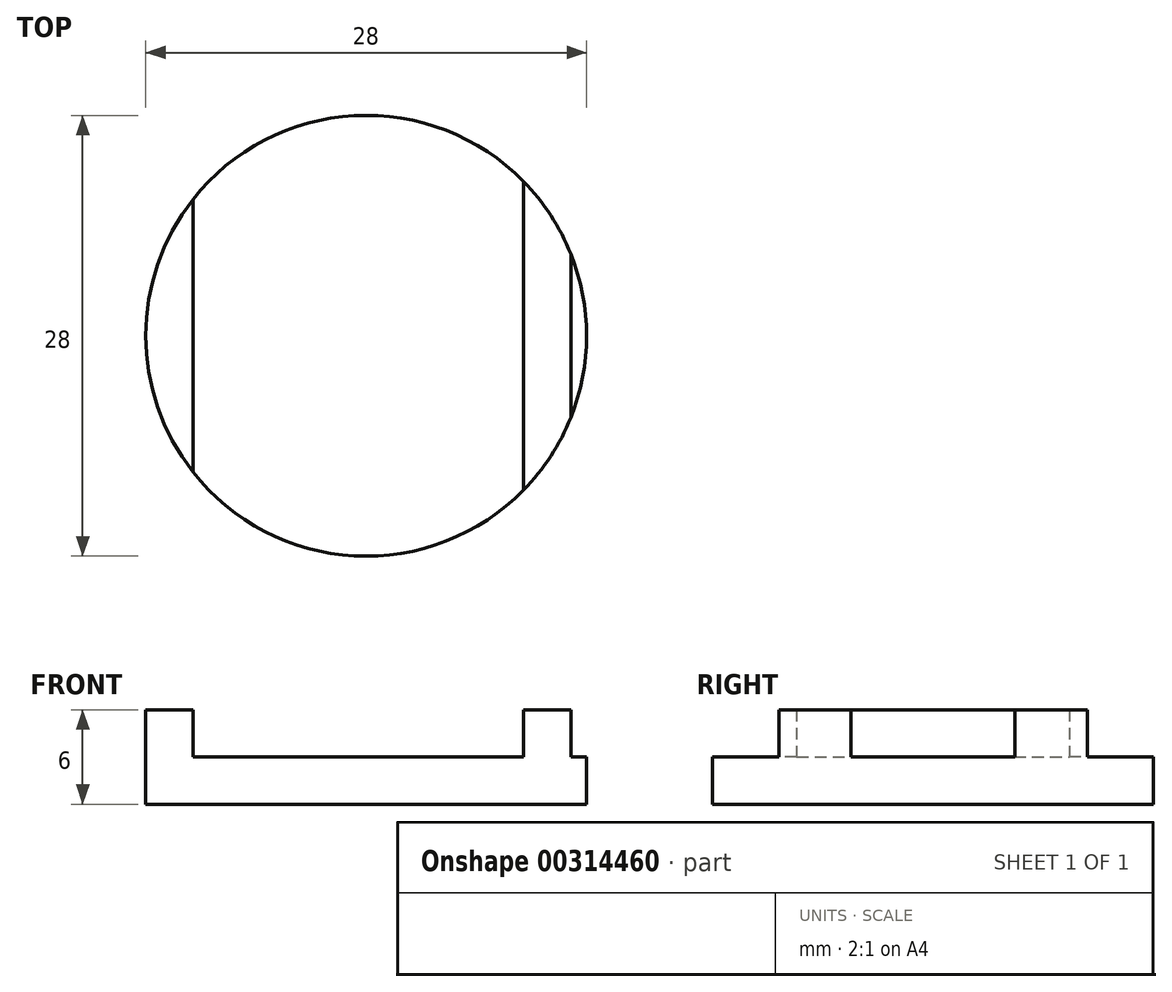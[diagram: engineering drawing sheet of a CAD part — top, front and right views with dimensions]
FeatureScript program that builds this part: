
annotation { "Feature Type Name" : "Feature", "Feature Type Description" : "" }
export const myFeature = defineFeature(function(context is Context, id is Id, definition is map)
    precondition{}
    {
        {
            var Q0;
            Q0=qCreatedBy(makeId("Top.planeOp"),FACE);
            var sketch = newSketch(context, id + "F0", { "sketchPlane" : qUnion([Q0])});
            skCircle(sketch, "E0", {"center": v(0, 0) * mm, "radius": 14 * mm});
            skSolve(sketch);
        }
        {
            var Q0;
            Q0=makeQuery(id+"F0.imprint","IMPRINT",FACE,{"disambiguationData":[TD([[makeQuery(id+"F0.imprint","IMPRINT",EDGE,{"derivedFrom":sQuery(id+"F0.wireOp",EDGE,"E0")}),1.0]])]});
            extrude(context, id + "F1", {"entities" : qUnion([Q0]), "depth" : 3 * mm});
        }
        {
            var Q0;
            Q0=makeQuery(id+"F1.opExtrude","CAP_FACE",FACE,{"disambiguationData":[OSD([sQuery(id+"F0.wireOp",EDGE,"E0")])],"isStart":false});
            var sketch = newSketch(context, id + "F2", { "sketchPlane" : qUnion([Q0])});
            skLineSegment(sketch, "E1.bottom", {"start": v(-11, -14) * mm, "end": v(-14, -14) * mm});
            skLineSegment(sketch, "E1.top", {"start": v(-11, 14) * mm, "end": v(-14, 14) * mm});
            skLineSegment(sketch, "E1.left", {"start": v(-11, -14) * mm, "end": v(-11, 14) * mm});
            skLineSegment(sketch, "E1.right", {"start": v(-14, -14) * mm, "end": v(-14, 14) * mm});
            skPoint(sketch, "E1.middle", {"position": v(-12.5, 0) * mm});
            skLineSegment(sketch, "E2.1.0.0", {"start": v(-8, -14) * mm, "end": v(-11, -14) * mm});
            skLineSegment(sketch, "E2.1.0.1", {"start": v(-8, 14) * mm, "end": v(-11, 14) * mm});
            skLineSegment(sketch, "E2.1.0.2", {"start": v(-8, -14) * mm, "end": v(-8, 14) * mm});
            skPoint(sketch, "E2.1.0.4", {"position": v(-9.5, 0) * mm});
            skLineSegment(sketch, "E2.2.0.0", {"start": v(-5, -14) * mm, "end": v(-8, -14) * mm});
            skLineSegment(sketch, "E2.2.0.1", {"start": v(-5, 14) * mm, "end": v(-8, 14) * mm});
            skLineSegment(sketch, "E2.2.0.2", {"start": v(-5, -14) * mm, "end": v(-5, 14) * mm});
            skLineSegment(sketch, "E2.2.0.3", {"start": v(-8, -14) * mm, "end": v(-8, 14) * mm});
            skPoint(sketch, "E2.2.0.4", {"position": v(-6.5, 0) * mm});
            skLineSegment(sketch, "E2.direction1", {"start": v(-14, -14) * mm, "end": v(-11, -14) * mm, "construction": true});
            skLineSegment(sketch, "E3.0.3.0", {"start": v(-2, -14) * mm, "end": v(-5, -14) * mm});
            skLineSegment(sketch, "E3.3.3.0", {"start": v(-2, 14) * mm, "end": v(-5, 14) * mm});
            skLineSegment(sketch, "E3.6.3.0", {"start": v(-2, -14) * mm, "end": v(-2, 14) * mm});
            skPoint(sketch, "E3.12.3.0", {"position": v(-3.5, 0) * mm});
            skLineSegment(sketch, "E3.0.4.0", {"start": v(1, -14) * mm, "end": v(-2, -14) * mm});
            skLineSegment(sketch, "E3.3.4.0", {"start": v(1, 14) * mm, "end": v(-2, 14) * mm});
            skLineSegment(sketch, "E3.6.4.0", {"start": v(1, -14) * mm, "end": v(1, 14) * mm});
            skLineSegment(sketch, "E3.9.4.0", {"start": v(-2, -14) * mm, "end": v(-2, 14) * mm});
            skPoint(sketch, "E3.12.4.0", {"position": v(-0.5, 0) * mm});
            skLineSegment(sketch, "E3.0.5.0", {"start": v(4, -14) * mm, "end": v(1, -14) * mm});
            skLineSegment(sketch, "E3.3.5.0", {"start": v(4, 14) * mm, "end": v(1, 14) * mm});
            skLineSegment(sketch, "E3.6.5.0", {"start": v(4, -14) * mm, "end": v(4, 14) * mm});
            skLineSegment(sketch, "E3.9.5.0", {"start": v(1, -14) * mm, "end": v(1, 14) * mm});
            skPoint(sketch, "E3.12.5.0", {"position": v(2.5, 0) * mm});
            skLineSegment(sketch, "E3.0.6.0", {"start": v(7, -14) * mm, "end": v(4, -14) * mm});
            skLineSegment(sketch, "E3.3.6.0", {"start": v(7, 14) * mm, "end": v(4, 14) * mm});
            skLineSegment(sketch, "E3.6.6.0", {"start": v(7, -14) * mm, "end": v(7, 14) * mm});
            skLineSegment(sketch, "E3.9.6.0", {"start": v(4, -14) * mm, "end": v(4, 14) * mm});
            skPoint(sketch, "E3.12.6.0", {"position": v(5.5, 0) * mm});
            skLineSegment(sketch, "E3.0.7.0", {"start": v(10, -14) * mm, "end": v(7, -14) * mm});
            skLineSegment(sketch, "E3.3.7.0", {"start": v(10, 14) * mm, "end": v(7, 14) * mm});
            skLineSegment(sketch, "E3.6.7.0", {"start": v(10, -14) * mm, "end": v(10, 14) * mm});
            skLineSegment(sketch, "E3.9.7.0", {"start": v(7, -14) * mm, "end": v(7, 14) * mm});
            skPoint(sketch, "E3.12.7.0", {"position": v(8.5, 0) * mm});
            skLineSegment(sketch, "E4.0.8.0", {"start": v(13, -14) * mm, "end": v(10, -14) * mm});
            skLineSegment(sketch, "E4.3.8.0", {"start": v(13, 14) * mm, "end": v(10, 14) * mm});
            skLineSegment(sketch, "E4.6.8.0", {"start": v(13, -14) * mm, "end": v(13, 14) * mm});
            skPoint(sketch, "E4.12.8.0", {"position": v(11.5, 0) * mm});
            skLineSegment(sketch, "E4.0.9.0", {"start": v(16, -14) * mm, "end": v(13, -14) * mm});
            skLineSegment(sketch, "E4.3.9.0", {"start": v(16, 14) * mm, "end": v(13, 14) * mm});
            skLineSegment(sketch, "E4.6.9.0", {"start": v(16, -14) * mm, "end": v(16, 14) * mm});
            skLineSegment(sketch, "E4.9.9.0", {"start": v(13, -14) * mm, "end": v(13, 14) * mm});
            skPoint(sketch, "E4.12.9.0", {"position": v(14.5, 0) * mm});
            skLineSegment(sketch, "E4.0.10.0", {"start": v(19, -14) * mm, "end": v(16, -14) * mm});
            skLineSegment(sketch, "E4.3.10.0", {"start": v(19, 14) * mm, "end": v(16, 14) * mm});
            skLineSegment(sketch, "E4.6.10.0", {"start": v(19, -14) * mm, "end": v(19, 14) * mm});
            skLineSegment(sketch, "E4.9.10.0", {"start": v(16, -14) * mm, "end": v(16, 14) * mm});
            skPoint(sketch, "E4.12.10.0", {"position": v(17.5, 0) * mm});
            skLineSegment(sketch, "E4.0.11.0", {"start": v(22, -14) * mm, "end": v(19, -14) * mm});
            skLineSegment(sketch, "E4.3.11.0", {"start": v(22, 14) * mm, "end": v(19, 14) * mm});
            skLineSegment(sketch, "E4.6.11.0", {"start": v(22, -14) * mm, "end": v(22, 14) * mm});
            skLineSegment(sketch, "E4.9.11.0", {"start": v(19, -14) * mm, "end": v(19, 14) * mm});
            skPoint(sketch, "E4.12.11.0", {"position": v(20.5, 0) * mm});
            skLineSegment(sketch, "E4.0.12.0", {"start": v(25, -14) * mm, "end": v(22, -14) * mm});
            skLineSegment(sketch, "E4.3.12.0", {"start": v(25, 14) * mm, "end": v(22, 14) * mm});
            skLineSegment(sketch, "E4.6.12.0", {"start": v(25, -14) * mm, "end": v(25, 14) * mm});
            skLineSegment(sketch, "E4.9.12.0", {"start": v(22, -14) * mm, "end": v(22, 14) * mm});
            skPoint(sketch, "E4.12.12.0", {"position": v(23.5, 0) * mm});
            skLineSegment(sketch, "E4.0.13.0", {"start": v(28, -14) * mm, "end": v(25, -14) * mm});
            skLineSegment(sketch, "E4.3.13.0", {"start": v(28, 14) * mm, "end": v(25, 14) * mm});
            skLineSegment(sketch, "E4.6.13.0", {"start": v(28, -14) * mm, "end": v(28, 14) * mm});
            skLineSegment(sketch, "E4.9.13.0", {"start": v(25, -14) * mm, "end": v(25, 14) * mm});
            skPoint(sketch, "E4.12.13.0", {"position": v(26.5, 0) * mm});
            skSolve(sketch);
        }
        {
            var Q0;
            {var subQ0=sQuery(id+"F2.wireOp",EDGE,"E3.9.4.0");var subQ1=makeQuery(id+"F1.opExtrude","CAP_EDGE",EDGE,{"disambiguationData":[OSD([sQuery(id+"F0.wireOp",EDGE,"E0")])],"isStart":false});var subQ2=makeQuery(id+"F2.imprint","INTERSECT",VERTEX,{"disambiguationData":[OD(0.0)],"derivedFrom":[subQ1,subQ0]});Q0=makeQuery(id+"F2.imprint","IMPRINT",FACE,{"disambiguationData":[TD([[makeQuery(id+"F2.imprint","IMPRINT",EDGE,{"disambiguationData":[TD([[subQ2,-1.0]])],"derivedFrom":subQ0}),-1.0]])]});}
            var Q1;
            {var subQ0=sQuery(id+"F2.wireOp",EDGE,"E1.left");var subQ1=makeQuery(id+"F1.opExtrude","CAP_EDGE",EDGE,{"disambiguationData":[OSD([sQuery(id+"F0.wireOp",EDGE,"E0")])],"isStart":false});var subQ2=makeQuery(id+"F2.imprint","INTERSECT",VERTEX,{"disambiguationData":[OD(0.0)],"derivedFrom":[subQ1,subQ0]});Q1=makeQuery(id+"F2.imprint","IMPRINT",FACE,{"disambiguationData":[TD([[makeQuery(id+"F2.imprint","IMPRINT",EDGE,{"disambiguationData":[TD([[subQ2,-1.0]])],"derivedFrom":subQ0}),1.0]])]});}
            var Q2;
            {var subQ0=sQuery(id+"F2.wireOp",EDGE,"E2.2.0.3");var subQ1=makeQuery(id+"F1.opExtrude","CAP_EDGE",EDGE,{"disambiguationData":[OSD([sQuery(id+"F0.wireOp",EDGE,"E0")])],"isStart":false});var subQ2=makeQuery(id+"F2.imprint","INTERSECT",VERTEX,{"disambiguationData":[OD(0.0)],"derivedFrom":[subQ1,subQ0]});Q2=makeQuery(id+"F2.imprint","IMPRINT",FACE,{"disambiguationData":[TD([[makeQuery(id+"F2.imprint","IMPRINT",EDGE,{"disambiguationData":[TD([[subQ2,-1.0]])],"derivedFrom":subQ0}),-1.0]])]});}
            var Q3;
            {var subQ0=sQuery(id+"F2.wireOp",EDGE,"E3.9.6.0");var subQ1=makeQuery(id+"F1.opExtrude","CAP_EDGE",EDGE,{"disambiguationData":[OSD([sQuery(id+"F0.wireOp",EDGE,"E0")])],"isStart":false});var subQ2=makeQuery(id+"F2.imprint","INTERSECT",VERTEX,{"disambiguationData":[OD(0.0)],"derivedFrom":[subQ1,subQ0]});Q3=makeQuery(id+"F2.imprint","IMPRINT",FACE,{"disambiguationData":[TD([[makeQuery(id+"F2.imprint","IMPRINT",EDGE,{"disambiguationData":[TD([[subQ2,-1.0]])],"derivedFrom":subQ0}),-1.0]])]});}
            var Q4;
            {var subQ0=sQuery(id+"F2.wireOp",EDGE,"E3.6.7.0");var subQ1=makeQuery(id+"F1.opExtrude","CAP_EDGE",EDGE,{"disambiguationData":[OSD([sQuery(id+"F0.wireOp",EDGE,"E0")])],"isStart":false});var subQ2=makeQuery(id+"F2.imprint","INTERSECT",VERTEX,{"disambiguationData":[OD(0.0)],"derivedFrom":[subQ1,subQ0]});Q4=makeQuery(id+"F2.imprint","IMPRINT",FACE,{"disambiguationData":[TD([[makeQuery(id+"F2.imprint","IMPRINT",EDGE,{"disambiguationData":[TD([[subQ2,-1.0]])],"derivedFrom":subQ0}),-1.0]])]});}
            extrude(context, id + "F3", {"entities" : qUnion([Q0, Q1, Q2, Q3, Q4]), "operationType" : NewBodyOperationType.ADD, "depth" : 3 * mm});
        }
    });
